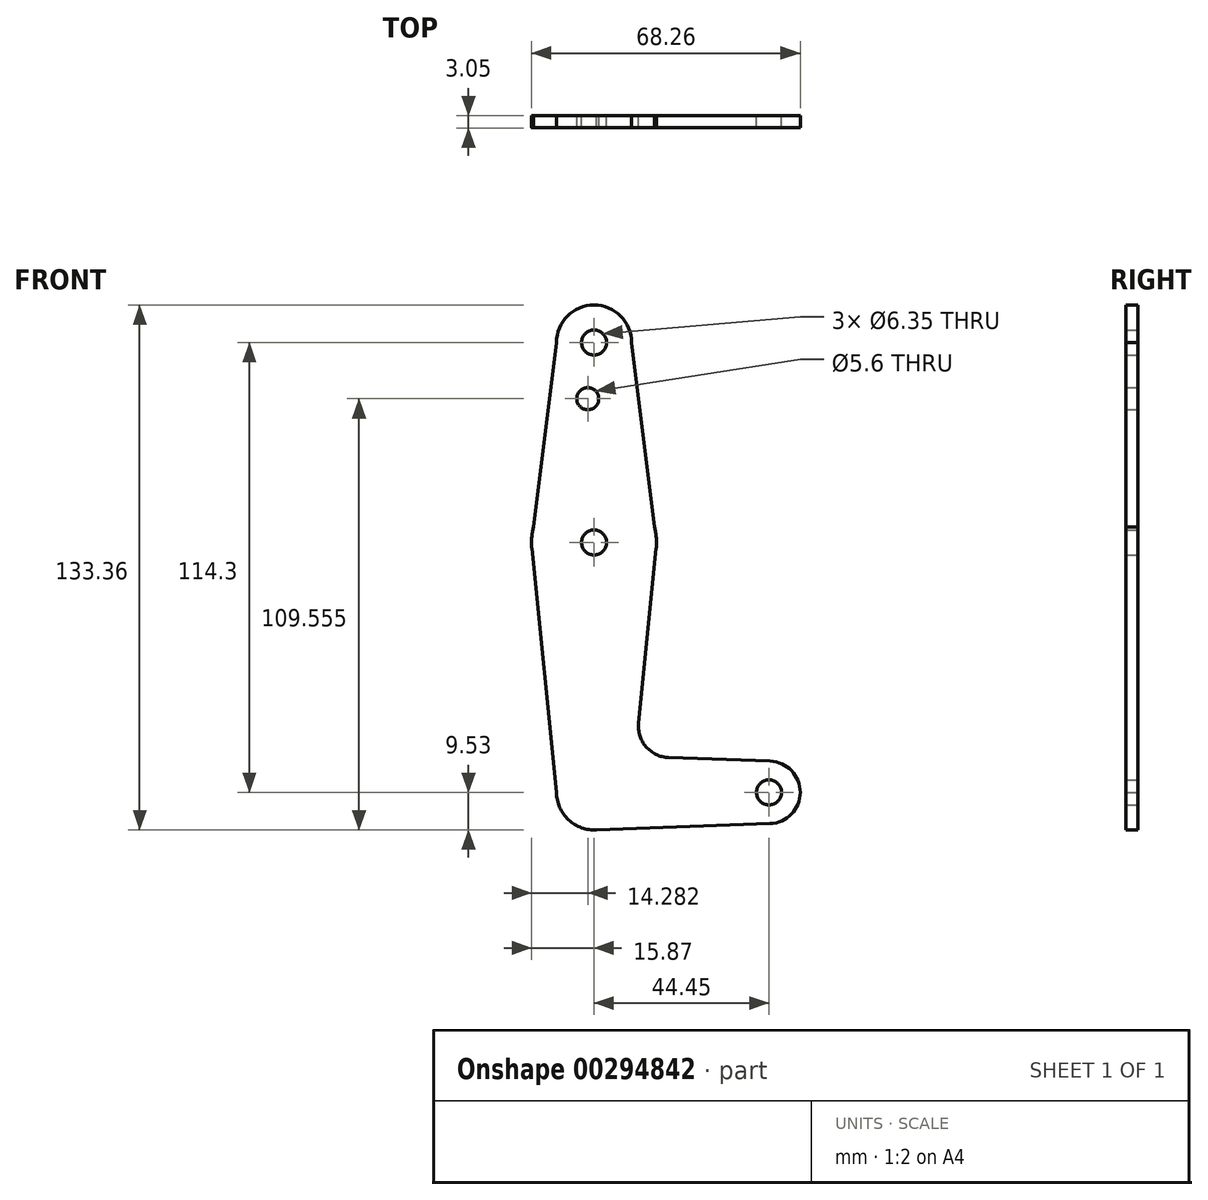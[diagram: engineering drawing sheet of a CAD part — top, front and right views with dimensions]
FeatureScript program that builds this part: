
annotation { "Feature Type Name" : "Feature", "Feature Type Description" : "" }
export const myFeature = defineFeature(function(context is Context, id is Id, definition is map)
    precondition{}
    {
        {
            var Q0;
            Q0=qCreatedBy(makeId("Front.planeOp"),FACE);
            var sketch = newSketch(context, id + "F0", { "sketchPlane" : qUnion([Q0])});
            skCircle(sketch, "E0", {"center": v(0, 0) * mm, "radius": 9.53 * mm});
            skCircle(sketch, "E1", {"center": v(0, 63.5) * mm, "radius": 15.88 * mm});
            skCircle(sketch, "E2", {"center": v(44.45, 0) * mm, "radius": 7.94 * mm});
            skCircle(sketch, "E3", {"center": v(0, 114.3) * mm, "radius": 9.53 * mm});
            skLineSegment(sketch, "E4", {"start": v(0, 114.3) * mm, "end": v(0, 63.5) * mm, "construction": true});
            skLineSegment(sketch, "E5", {"start": v(0, 0) * mm, "end": v(0, 63.5) * mm, "construction": true});
            skLineSegment(sketch, "E6", {"start": v(0, 0) * mm, "end": v(44.45, 0) * mm, "construction": true});
            skLineSegment(sketch, "E7", {"start": v(18.93, 8.85) * mm, "end": v(44.73, 7.93) * mm});
            skLineSegment(sketch, "E8", {"start": v(0, -9.53) * mm, "end": v(44.73, -7.93) * mm});
            skLineSegment(sketch, "E9", {"start": v(-15.8, 61.9) * mm, "end": v(-9.52, 0) * mm});
            skLineSegment(sketch, "E10", {"start": v(15.8, 61.9) * mm, "end": v(11.3, 17.6) * mm});
            skLineSegment(sketch, "E11", {"start": v(-9.52, 114.3) * mm, "end": v(-15.87, 63.5) * mm});
            skLineSegment(sketch, "E12", {"start": v(9.52, 114.3) * mm, "end": v(15.88, 63.5) * mm});
            skCircle(sketch, "E13", {"center": v(0, 114.3) * mm, "radius": 3.18 * mm});
            skCircle(sketch, "E14", {"center": v(44.45, 0) * mm, "radius": 3.18 * mm});
            skCircle(sketch, "E15", {"center": v(0, 63.5) * mm, "radius": 3.18 * mm});
            skArc(sketch, "E16.filletArc", {"start": v(11.3, 17.6) * mm, "mid": v(13.22, 11.57) * mm, "end": v(18.93, 8.85) * mm});
            skCircle(sketch, "E17", {"center": v(-1.59, 100.03) * mm, "radius": 2.8 * mm});
            skSolve(sketch);
        }
        {
            var Q0;
            Q0 = qSketchRegion(id + "F0", true);
            extrude(context, id + "F1", {"entities" : qUnion([Q0]), "depth" : 3.05 * mm});
        }
    });
